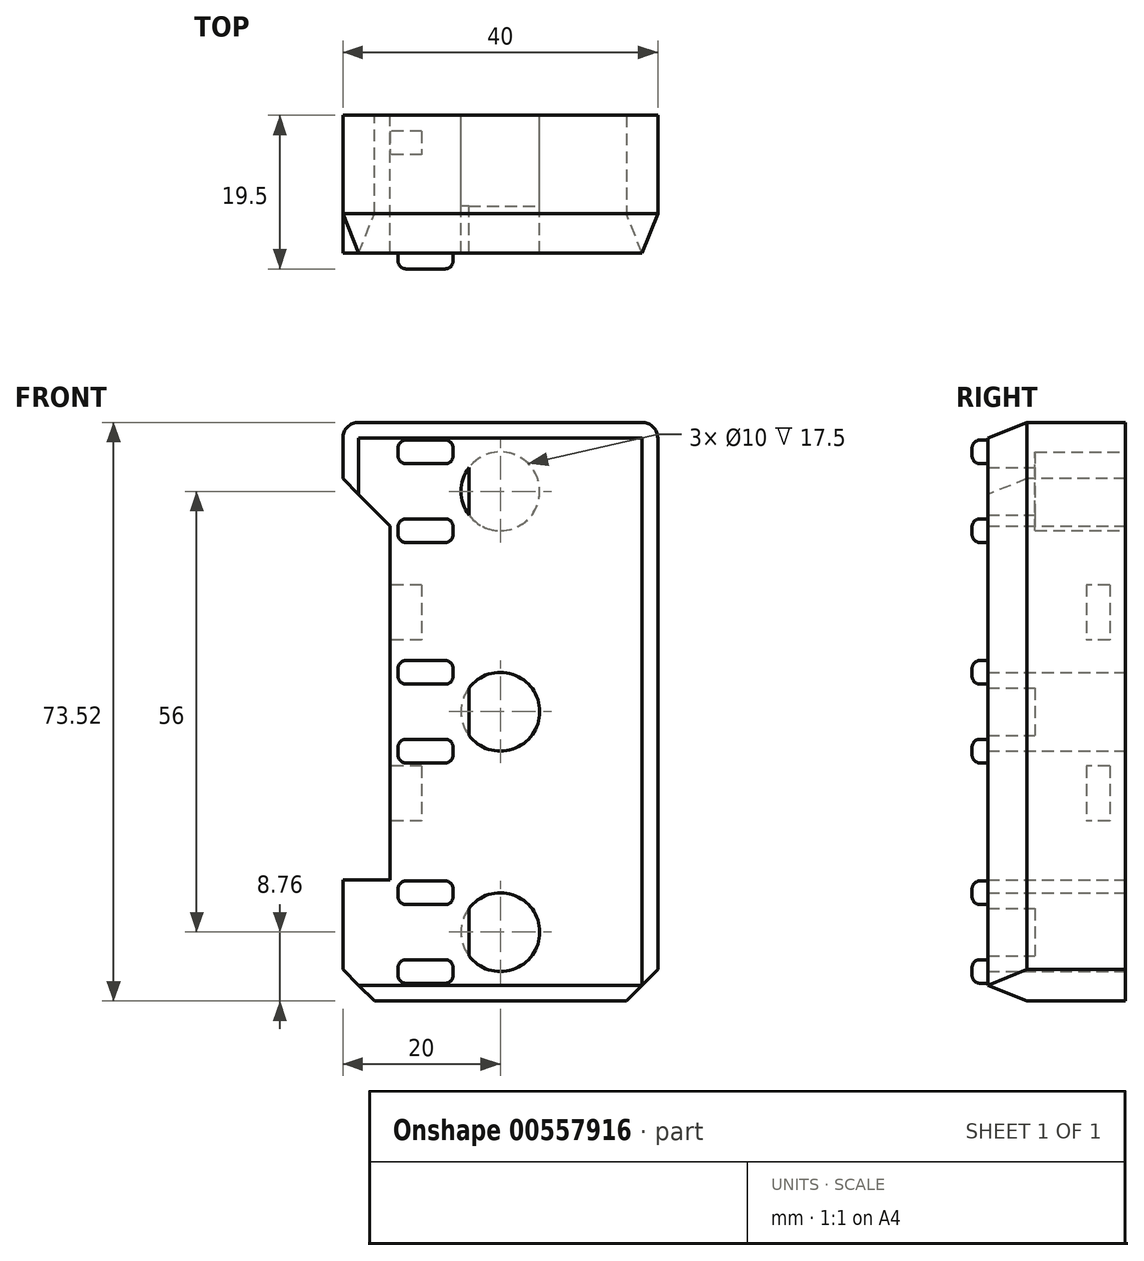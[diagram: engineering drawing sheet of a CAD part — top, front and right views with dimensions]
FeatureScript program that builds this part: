
annotation { "Feature Type Name" : "Feature", "Feature Type Description" : "" }
export const myFeature = defineFeature(function(context is Context, id is Id, definition is map)
    precondition{}
    {
        {
            var Q0;
            Q0=qCreatedBy(makeId("Front.planeOp"),FACE);
            var sketch = newSketch(context, id + "F0", { "sketchPlane" : qUnion([Q0])});
            skLineSegment(sketch, "E0.bottom", {"start": v(-20, 36.76) * mm, "end": v(20, 36.76) * mm});
            skLineSegment(sketch, "E0.top", {"start": v(-20, -36.76) * mm, "end": v(20, -36.76) * mm});
            skLineSegment(sketch, "E0.left", {"start": v(-20, 36.76) * mm, "end": v(-20, -36.76) * mm});
            skLineSegment(sketch, "E0.right", {"start": v(20, 36.76) * mm, "end": v(20, -36.76) * mm});
            skCircle(sketch, "E1", {"center": v(0, 0) * mm, "radius": 5 * mm});
            skCircle(sketch, "E2", {"center": v(0, 28) * mm, "radius": 5 * mm});
            skPoint(sketch, "E2.centerSnap0", {"position": v(0, 36.76) * mm});
            skCircle(sketch, "E3", {"center": v(0, -28) * mm, "radius": 5 * mm});
            skLineSegment(sketch, "E4", {"start": v(-4, 36.76) * mm, "end": v(-4, -36.76) * mm});
            skSolve(sketch);
        }
        {
            var Q0;
            {var subQ4=sQuery(id+"F0.wireOp",EDGE,"E0.left");Q0=makeQuery(id+"F0.imprint","IMPRINT",FACE,{"disambiguationData":[TD([[makeQuery(id+"F0.imprint","IMPRINT",EDGE,{"derivedFrom":subQ4}),1.0]])]});}
            var Q1;
            {var subQ8=sQuery(id+"F0.wireOp",EDGE,"E0.right");Q1=makeQuery(id+"F0.imprint","IMPRINT",FACE,{"disambiguationData":[TD([[makeQuery(id+"F0.imprint","IMPRINT",EDGE,{"derivedFrom":subQ8}),-1.0]])]});}
            var Q2;
            {var subQ0=sQuery(id+"F0.wireOp",EDGE,"E4");var subQ1=sQuery(id+"F0.wireOp",EDGE,"E2");var subQ2=makeQuery(id+"F0.imprint","INTERSECT",VERTEX,{"disambiguationData":[OD(0.0)],"derivedFrom":[subQ1,subQ0]});Q2=makeQuery(id+"F0.imprint","IMPRINT",FACE,{"disambiguationData":[TD([[makeQuery(id+"F0.imprint","IMPRINT",EDGE,{"disambiguationData":[TD([[subQ2,-1.0]])],"derivedFrom":subQ1}),1.0]])]});}
            var Q3;
            {var subQ0=sQuery(id+"F0.wireOp",EDGE,"E4");var subQ1=sQuery(id+"F0.wireOp",EDGE,"E1");var subQ2=makeQuery(id+"F0.imprint","INTERSECT",VERTEX,{"disambiguationData":[OD(0.0)],"derivedFrom":[subQ1,subQ0]});Q3=makeQuery(id+"F0.imprint","IMPRINT",FACE,{"disambiguationData":[TD([[makeQuery(id+"F0.imprint","IMPRINT",EDGE,{"disambiguationData":[TD([[subQ2,-1.0]])],"derivedFrom":subQ1}),1.0]])]});}
            var Q4;
            {var subQ0=sQuery(id+"F0.wireOp",EDGE,"E4");var subQ1=sQuery(id+"F0.wireOp",EDGE,"E3");var subQ2=makeQuery(id+"F0.imprint","INTERSECT",VERTEX,{"disambiguationData":[OD(0.0)],"derivedFrom":[subQ1,subQ0]});Q4=makeQuery(id+"F0.imprint","IMPRINT",FACE,{"disambiguationData":[TD([[makeQuery(id+"F0.imprint","IMPRINT",EDGE,{"disambiguationData":[TD([[subQ2,-1.0]])],"derivedFrom":subQ1}),1.0]])]});}
            extrude(context, id + "F1", {"entities" : qUnion([Q0, Q1, Q2, Q3, Q4]), "depth" : 6 * mm, "offsetDistance" : 25 * mm});
        }
        {
            var Q0;
            {var subQ8=sQuery(id+"F0.wireOp",EDGE,"E0.right");Q0=makeQuery(id+"F0.imprint","IMPRINT",FACE,{"disambiguationData":[TD([[makeQuery(id+"F0.imprint","IMPRINT",EDGE,{"derivedFrom":subQ8}),-1.0]])]});}
            var Q1;
            {var subQ4=sQuery(id+"F0.wireOp",EDGE,"E0.left");Q1=makeQuery(id+"F0.imprint","IMPRINT",FACE,{"disambiguationData":[TD([[makeQuery(id+"F0.imprint","IMPRINT",EDGE,{"derivedFrom":subQ4}),1.0]])]});}
            extrude(context, id + "F2", {"entities" : qUnion([Q0, Q1]), "operationType" : NewBodyOperationType.ADD, "oppositeDirection" : true, "depth" : 11.5 * mm, "offsetDistance" : 25 * mm});
        }
        {
            var Q0;
            {var subQ0=sQuery(id+"F0.wireOp",EDGE,"E0.right");var subQ1=sQuery(id+"F0.wireOp",EDGE,"E0.top");Q0=makeQuery(id+"F2.boolean.opBoolean","MERGE",EDGE,{"derivedFrom":[makeQuery(id+"F1.opExtrude","SWEPT_EDGE",EDGE,{"disambiguationData":[OSD([subQ1,subQ0])]}),makeQuery(id+"F2.opExtrude","SWEPT_EDGE",EDGE,{"disambiguationData":[OSD([subQ1,subQ0])]})]});}
            var Q1;
            {var subQ0=sQuery(id+"F0.wireOp",EDGE,"E0.left");var subQ1=sQuery(id+"F0.wireOp",EDGE,"E0.top");Q1=makeQuery(id+"F2.boolean.opBoolean","MERGE",EDGE,{"derivedFrom":[makeQuery(id+"F1.opExtrude","SWEPT_EDGE",EDGE,{"disambiguationData":[OSD([subQ1,subQ0])]}),makeQuery(id+"F2.opExtrude","SWEPT_EDGE",EDGE,{"disambiguationData":[OSD([subQ1,subQ0])]})]});}
            chamfer(context, id + "F3", {"entities" : qUnion([Q0, Q1]), "width" : 4 * mm, "tangentPropagation" : true});
        }
        {
            var Q0;
            Q0=qCreatedBy(makeId("Front.planeOp"),FACE);
            var sketch = newSketch(context, id + "F4", { "sketchPlane" : qUnion([Q0])});
            skLineSegment(sketch, "E5.bottom", {"start": v(-20, 23.61) * mm, "end": v(-14, 23.61) * mm});
            skLineSegment(sketch, "E5.top", {"start": v(-20, -21.39) * mm, "end": v(-14, -21.39) * mm});
            skLineSegment(sketch, "E5.left", {"start": v(-20, 23.61) * mm, "end": v(-20, -21.39) * mm});
            skLineSegment(sketch, "E5.right", {"start": v(-14, 23.61) * mm, "end": v(-14, -21.39) * mm});
            skSolve(sketch);
        }
        {
            var Q0;
            Q0 = qSketchRegion(id + "F4", true);
            extrude(context, id + "F5", {"entities" : qUnion([Q0]), "operationType" : NewBodyOperationType.REMOVE, "endBound" : BoundingType.SYMMETRIC, "depth" : 50 * mm, "offsetDistance" : 25 * mm});
        }
        {
            var Q0;
            Q0=makeQuery(id+"F5.boolean.opBoolean","COPY",EDGE,{"derivedFrom":makeQuery(id+"F5.opExtrude","SWEPT_EDGE",EDGE,{"disambiguationData":[OSD([sQuery(id+"F4.wireOp",EDGE,"E5.bottom"),sQuery(id+"F4.wireOp",EDGE,"E5.left")])]})});
            var Q1;
            Q1=makeQuery(id+"F5.boolean.opBoolean","COPY",EDGE,{"derivedFrom":makeQuery(id+"F5.opExtrude","SWEPT_EDGE",EDGE,{"disambiguationData":[OSD([sQuery(id+"F4.wireOp",EDGE,"E5.top"),sQuery(id+"F4.wireOp",EDGE,"E5.left")])]})});
            chamfer(context, id + "F6", {"entities" : qUnion([Q0, Q1]), "width" : 6 * mm, "tangentPropagation" : true});
        }
        {
            var Q0;
            Q0=qCreatedBy(makeId("Right.planeOp"),FACE);
            var sketch = newSketch(context, id + "F7", { "sketchPlane" : qUnion([Q0])});
            skLineSegment(sketch, "E6.bottom", {"start": v(-6, 34.5) * mm, "end": v(-8, 34.5) * mm});
            skLineSegment(sketch, "E6.top", {"start": v(-6, 31.5) * mm, "end": v(-8, 31.5) * mm});
            skLineSegment(sketch, "E6.left", {"start": v(-6, 34.5) * mm, "end": v(-6, 31.5) * mm});
            skLineSegment(sketch, "E6.right", {"start": v(-8, 34.5) * mm, "end": v(-8, 31.5) * mm});
            skLineSegment(sketch, "E7.bottom", {"start": v(-6, 24.5) * mm, "end": v(-8, 24.5) * mm});
            skLineSegment(sketch, "E7.top", {"start": v(-6, 21.5) * mm, "end": v(-8, 21.5) * mm});
            skLineSegment(sketch, "E7.left", {"start": v(-6, 24.5) * mm, "end": v(-6, 21.5) * mm});
            skLineSegment(sketch, "E7.right", {"start": v(-8, 24.5) * mm, "end": v(-8, 21.5) * mm});
            skLineSegment(sketch, "E8.bottom", {"start": v(-6, 6.5) * mm, "end": v(-8, 6.5) * mm});
            skLineSegment(sketch, "E8.top", {"start": v(-6, 3.5) * mm, "end": v(-8, 3.5) * mm});
            skLineSegment(sketch, "E8.left", {"start": v(-6, 6.5) * mm, "end": v(-6, 3.5) * mm});
            skLineSegment(sketch, "E8.right", {"start": v(-8, 6.5) * mm, "end": v(-8, 3.5) * mm});
            skLineSegment(sketch, "E9.bottom", {"start": v(-6, -3.5) * mm, "end": v(-8, -3.5) * mm});
            skLineSegment(sketch, "E9.top", {"start": v(-6, -6.5) * mm, "end": v(-8, -6.5) * mm});
            skLineSegment(sketch, "E9.left", {"start": v(-6, -3.5) * mm, "end": v(-6, -6.5) * mm});
            skLineSegment(sketch, "E9.right", {"start": v(-8, -3.5) * mm, "end": v(-8, -6.5) * mm});
            skLineSegment(sketch, "E10.bottom", {"start": v(-6, -21.5) * mm, "end": v(-8, -21.5) * mm});
            skLineSegment(sketch, "E10.top", {"start": v(-6, -24.5) * mm, "end": v(-8, -24.5) * mm});
            skLineSegment(sketch, "E10.left", {"start": v(-6, -21.5) * mm, "end": v(-6, -24.5) * mm});
            skLineSegment(sketch, "E10.right", {"start": v(-8, -21.5) * mm, "end": v(-8, -24.5) * mm});
            skLineSegment(sketch, "E11.bottom", {"start": v(-6, -31.5) * mm, "end": v(-8, -31.5) * mm});
            skLineSegment(sketch, "E11.top", {"start": v(-6, -34.5) * mm, "end": v(-8, -34.5) * mm});
            skLineSegment(sketch, "E11.left", {"start": v(-6, -31.5) * mm, "end": v(-6, -34.5) * mm});
            skLineSegment(sketch, "E11.right", {"start": v(-8, -31.5) * mm, "end": v(-8, -34.5) * mm});
            skSolve(sketch);
        }
        {
            var Q0;
            Q0 = qSketchRegion(id + "F7", true);
            extrude(context, id + "F8", {"entities" : qUnion([Q0]), "operationType" : NewBodyOperationType.ADD, "oppositeDirection" : true, "depth" : 13 * mm, "offsetDistance" : 25 * mm, "hasSecondDirection" : true, "secondDirectionOppositeDirection" : true, "secondDirectionDepth" : 6 * mm});
        }
        {
            var Q0;
            Q0=makeQuery(id+"F8.opExtrude","CAP_EDGE",EDGE,{"disambiguationData":[OSD([sQuery(id+"F7.wireOp",EDGE,"E11.top")])],"isStart":false});
            fillet(context, id + "F9", {"entities" : qUnion([Q0]), "radius" : 1 * mm, "tangentPropagation" : true, "allowEdgeOverflow" : false});
        }
        {
            var Q0;
            Q0=makeQuery(id+"F8.opExtrude","CAP_EDGE",EDGE,{"disambiguationData":[OSD([sQuery(id+"F7.wireOp",EDGE,"E11.top")])],"isStart":true});
            var Q1;
            Q1=makeQuery(id+"F8.opExtrude","CAP_EDGE",EDGE,{"disambiguationData":[OSD([sQuery(id+"F7.wireOp",EDGE,"E11.bottom")])],"isStart":false});
            var Q2;
            Q2=makeQuery(id+"F8.opExtrude","CAP_EDGE",EDGE,{"disambiguationData":[OSD([sQuery(id+"F7.wireOp",EDGE,"E11.bottom")])],"isStart":true});
            var Q3;
            Q3=makeQuery(id+"F8.opExtrude","SWEPT_EDGE",EDGE,{"disambiguationData":[OSD([sQuery(id+"F7.wireOp",EDGE,"E11.bottom"),sQuery(id+"F7.wireOp",EDGE,"E11.right")])]});
            var Q4;
            Q4=makeQuery(id+"F8.opExtrude","SWEPT_EDGE",EDGE,{"disambiguationData":[OSD([sQuery(id+"F7.wireOp",EDGE,"E11.top"),sQuery(id+"F7.wireOp",EDGE,"E11.right")])]});
            var Q5;
            Q5=makeQuery(id+"F8.opExtrude","CAP_EDGE",EDGE,{"disambiguationData":[OSD([sQuery(id+"F7.wireOp",EDGE,"E11.right")])],"isStart":true});
            var Q6;
            Q6=makeQuery(id+"F8.opExtrude","CAP_EDGE",EDGE,{"disambiguationData":[OSD([sQuery(id+"F7.wireOp",EDGE,"E10.top")])],"isStart":true});
            var Q7;
            Q7=makeQuery(id+"F8.opExtrude","CAP_EDGE",EDGE,{"disambiguationData":[OSD([sQuery(id+"F7.wireOp",EDGE,"E10.top")])],"isStart":false});
            var Q8;
            Q8=makeQuery(id+"F8.opExtrude","CAP_EDGE",EDGE,{"disambiguationData":[OSD([sQuery(id+"F7.wireOp",EDGE,"E10.bottom")])],"isStart":false});
            var Q9;
            Q9=makeQuery(id+"F8.opExtrude","CAP_EDGE",EDGE,{"disambiguationData":[OSD([sQuery(id+"F7.wireOp",EDGE,"E10.bottom")])],"isStart":true});
            var Q10;
            Q10=makeQuery(id+"F8.opExtrude","SWEPT_EDGE",EDGE,{"disambiguationData":[OSD([sQuery(id+"F7.wireOp",EDGE,"E10.bottom"),sQuery(id+"F7.wireOp",EDGE,"E10.right")])]});
            var Q11;
            Q11=makeQuery(id+"F8.opExtrude","SWEPT_EDGE",EDGE,{"disambiguationData":[OSD([sQuery(id+"F7.wireOp",EDGE,"E10.top"),sQuery(id+"F7.wireOp",EDGE,"E10.right")])]});
            var Q12;
            Q12=makeQuery(id+"F8.opExtrude","CAP_EDGE",EDGE,{"disambiguationData":[OSD([sQuery(id+"F7.wireOp",EDGE,"E10.right")])],"isStart":true});
            var Q13;
            Q13=makeQuery(id+"F8.opExtrude","CAP_EDGE",EDGE,{"disambiguationData":[OSD([sQuery(id+"F7.wireOp",EDGE,"E10.right")])],"isStart":false});
            var Q14;
            Q14=makeQuery(id+"F8.opExtrude","CAP_EDGE",EDGE,{"disambiguationData":[OSD([sQuery(id+"F7.wireOp",EDGE,"E9.top")])],"isStart":true});
            var Q15;
            Q15=makeQuery(id+"F8.opExtrude","CAP_EDGE",EDGE,{"disambiguationData":[OSD([sQuery(id+"F7.wireOp",EDGE,"E9.top")])],"isStart":false});
            var Q16;
            Q16=makeQuery(id+"F8.opExtrude","CAP_EDGE",EDGE,{"disambiguationData":[OSD([sQuery(id+"F7.wireOp",EDGE,"E9.bottom")])],"isStart":false});
            var Q17;
            Q17=makeQuery(id+"F8.opExtrude","CAP_EDGE",EDGE,{"disambiguationData":[OSD([sQuery(id+"F7.wireOp",EDGE,"E9.bottom")])],"isStart":true});
            var Q18;
            Q18=makeQuery(id+"F8.opExtrude","SWEPT_EDGE",EDGE,{"disambiguationData":[OSD([sQuery(id+"F7.wireOp",EDGE,"E9.top"),sQuery(id+"F7.wireOp",EDGE,"E9.right")])]});
            var Q19;
            Q19=makeQuery(id+"F8.opExtrude","SWEPT_EDGE",EDGE,{"disambiguationData":[OSD([sQuery(id+"F7.wireOp",EDGE,"E9.bottom"),sQuery(id+"F7.wireOp",EDGE,"E9.right")])]});
            var Q20;
            Q20=makeQuery(id+"F8.opExtrude","CAP_EDGE",EDGE,{"disambiguationData":[OSD([sQuery(id+"F7.wireOp",EDGE,"E9.right")])],"isStart":true});
            var Q21;
            Q21=makeQuery(id+"F8.opExtrude","CAP_EDGE",EDGE,{"disambiguationData":[OSD([sQuery(id+"F7.wireOp",EDGE,"E9.right")])],"isStart":false});
            var Q22;
            Q22=makeQuery(id+"F8.opExtrude","CAP_EDGE",EDGE,{"disambiguationData":[OSD([sQuery(id+"F7.wireOp",EDGE,"E8.top")])],"isStart":false});
            var Q23;
            Q23=makeQuery(id+"F8.opExtrude","CAP_EDGE",EDGE,{"disambiguationData":[OSD([sQuery(id+"F7.wireOp",EDGE,"E8.top")])],"isStart":true});
            var Q24;
            Q24=makeQuery(id+"F8.opExtrude","CAP_EDGE",EDGE,{"disambiguationData":[OSD([sQuery(id+"F7.wireOp",EDGE,"E8.bottom")])],"isStart":true});
            var Q25;
            Q25=makeQuery(id+"F8.opExtrude","CAP_EDGE",EDGE,{"disambiguationData":[OSD([sQuery(id+"F7.wireOp",EDGE,"E8.bottom")])],"isStart":false});
            var Q26;
            Q26=makeQuery(id+"F8.opExtrude","SWEPT_EDGE",EDGE,{"disambiguationData":[OSD([sQuery(id+"F7.wireOp",EDGE,"E8.bottom"),sQuery(id+"F7.wireOp",EDGE,"E8.right")])]});
            var Q27;
            Q27=makeQuery(id+"F8.opExtrude","SWEPT_EDGE",EDGE,{"disambiguationData":[OSD([sQuery(id+"F7.wireOp",EDGE,"E8.top"),sQuery(id+"F7.wireOp",EDGE,"E8.right")])]});
            var Q28;
            Q28=makeQuery(id+"F8.opExtrude","CAP_EDGE",EDGE,{"disambiguationData":[OSD([sQuery(id+"F7.wireOp",EDGE,"E8.right")])],"isStart":false});
            var Q29;
            Q29=makeQuery(id+"F8.opExtrude","CAP_EDGE",EDGE,{"disambiguationData":[OSD([sQuery(id+"F7.wireOp",EDGE,"E8.right")])],"isStart":true});
            var Q30;
            Q30=makeQuery(id+"F8.opExtrude","CAP_EDGE",EDGE,{"disambiguationData":[OSD([sQuery(id+"F7.wireOp",EDGE,"E7.top")])],"isStart":false});
            var Q31;
            Q31=makeQuery(id+"F8.opExtrude","CAP_EDGE",EDGE,{"disambiguationData":[OSD([sQuery(id+"F7.wireOp",EDGE,"E7.top")])],"isStart":true});
            var Q32;
            Q32=makeQuery(id+"F8.opExtrude","CAP_EDGE",EDGE,{"disambiguationData":[OSD([sQuery(id+"F7.wireOp",EDGE,"E7.bottom")])],"isStart":true});
            var Q33;
            Q33=makeQuery(id+"F8.opExtrude","CAP_EDGE",EDGE,{"disambiguationData":[OSD([sQuery(id+"F7.wireOp",EDGE,"E7.bottom")])],"isStart":false});
            var Q34;
            Q34=makeQuery(id+"F8.opExtrude","SWEPT_EDGE",EDGE,{"disambiguationData":[OSD([sQuery(id+"F7.wireOp",EDGE,"E7.bottom"),sQuery(id+"F7.wireOp",EDGE,"E7.right")])]});
            var Q35;
            Q35=makeQuery(id+"F8.opExtrude","SWEPT_EDGE",EDGE,{"disambiguationData":[OSD([sQuery(id+"F7.wireOp",EDGE,"E7.top"),sQuery(id+"F7.wireOp",EDGE,"E7.right")])]});
            var Q36;
            Q36=makeQuery(id+"F8.opExtrude","CAP_EDGE",EDGE,{"disambiguationData":[OSD([sQuery(id+"F7.wireOp",EDGE,"E7.right")])],"isStart":true});
            var Q37;
            Q37=makeQuery(id+"F8.opExtrude","CAP_EDGE",EDGE,{"disambiguationData":[OSD([sQuery(id+"F7.wireOp",EDGE,"E7.right")])],"isStart":false});
            var Q38;
            Q38=makeQuery(id+"F8.opExtrude","SWEPT_EDGE",EDGE,{"disambiguationData":[OSD([sQuery(id+"F7.wireOp",EDGE,"E6.top"),sQuery(id+"F7.wireOp",EDGE,"E6.right")])]});
            var Q39;
            Q39=makeQuery(id+"F8.opExtrude","CAP_EDGE",EDGE,{"disambiguationData":[OSD([sQuery(id+"F7.wireOp",EDGE,"E6.top")])],"isStart":false});
            var Q40;
            Q40=makeQuery(id+"F8.opExtrude","CAP_EDGE",EDGE,{"disambiguationData":[OSD([sQuery(id+"F7.wireOp",EDGE,"E6.top")])],"isStart":true});
            var Q41;
            Q41=makeQuery(id+"F8.opExtrude","CAP_EDGE",EDGE,{"disambiguationData":[OSD([sQuery(id+"F7.wireOp",EDGE,"E6.right")])],"isStart":true});
            var Q42;
            Q42=makeQuery(id+"F8.opExtrude","CAP_EDGE",EDGE,{"disambiguationData":[OSD([sQuery(id+"F7.wireOp",EDGE,"E6.right")])],"isStart":false});
            var Q43;
            Q43=makeQuery(id+"F8.opExtrude","SWEPT_EDGE",EDGE,{"disambiguationData":[OSD([sQuery(id+"F7.wireOp",EDGE,"E6.bottom"),sQuery(id+"F7.wireOp",EDGE,"E6.right")])]});
            var Q44;
            Q44=makeQuery(id+"F8.opExtrude","CAP_EDGE",EDGE,{"disambiguationData":[OSD([sQuery(id+"F7.wireOp",EDGE,"E6.bottom")])],"isStart":false});
            var Q45;
            Q45=makeQuery(id+"F8.opExtrude","CAP_EDGE",EDGE,{"disambiguationData":[OSD([sQuery(id+"F7.wireOp",EDGE,"E6.bottom")])],"isStart":true});
            fillet(context, id + "F10", {"entities" : qUnion([Q0, Q1, Q2, Q3, Q4, Q5, Q6, Q7, Q8, Q9, Q10, Q11, Q12, Q13, Q14, Q15, Q16, Q17, Q18, Q19, Q20, Q21, Q22, Q23, Q24, Q25, Q26, Q27, Q28, Q29, Q30, Q31, Q32, Q33, Q34, Q35, Q36, Q37, Q38, Q39, Q40, Q41, Q42, Q43, Q44, Q45]), "radius" : 1 * mm, "tangentPropagation" : true, "allowEdgeOverflow" : false});
        }
        {
            var Q0;
            {var subQ0=sQuery(id+"F0.wireOp",EDGE,"E0.left");var subQ1=sQuery(id+"F0.wireOp",EDGE,"E0.bottom");Q0=makeQuery(id+"F2.boolean.opBoolean","MERGE",EDGE,{"derivedFrom":[makeQuery(id+"F1.opExtrude","SWEPT_EDGE",EDGE,{"disambiguationData":[OSD([subQ1,subQ0])]}),makeQuery(id+"F2.opExtrude","SWEPT_EDGE",EDGE,{"disambiguationData":[OSD([subQ1,subQ0])]})]});}
            var Q1;
            {var subQ0=sQuery(id+"F0.wireOp",EDGE,"E0.right");var subQ1=sQuery(id+"F0.wireOp",EDGE,"E0.bottom");Q1=makeQuery(id+"F2.boolean.opBoolean","MERGE",EDGE,{"derivedFrom":[makeQuery(id+"F1.opExtrude","SWEPT_EDGE",EDGE,{"disambiguationData":[OSD([subQ1,subQ0])]}),makeQuery(id+"F2.opExtrude","SWEPT_EDGE",EDGE,{"disambiguationData":[OSD([subQ1,subQ0])]})]});}
            fillet(context, id + "F11", {"entities" : qUnion([Q0, Q1]), "radius" : 2 * mm, "tangentPropagation" : true, "allowEdgeOverflow" : false});
        }
        {
            var Q0;
            Q0=makeQuery(id+"F1.opExtrude","CAP_EDGE",EDGE,{"disambiguationData":[OSD([sQuery(id+"F0.wireOp",EDGE,"E0.right")])],"isStart":false});
            var Q1;
            Q1=makeQuery(id+"F1.opExtrude","CAP_EDGE",EDGE,{"disambiguationData":[OSD([sQuery(id+"F0.wireOp",EDGE,"E0.top")])],"isStart":false});
            chamfer(context, id + "F12", {"entities" : qUnion([Q0, Q1]), "chamferType" : ChamferType.TWO_OFFSETS, "width1" : 5 * mm, "oppositeDirection" : false, "width2" : 2 * mm, "tangentPropagation" : true});
        }
        {
            var Q0;
            Q0=makeQuery(id+"F5.boolean.opBoolean","COPY",FACE,{"derivedFrom":makeQuery(id+"F5.opExtrude","SWEPT_FACE",FACE,{"disambiguationData":[OSD([sQuery(id+"F4.wireOp",EDGE,"E5.right")])]})});
            var sketch = newSketch(context, id + "F13", { "sketchPlane" : qUnion([Q0])});
            skLineSegment(sketch, "E12.bottom", {"start": v(-9.5, 16.11) * mm, "end": v(-6.5, 16.11) * mm});
            skLineSegment(sketch, "E12.top", {"start": v(-9.5, 9.11) * mm, "end": v(-6.5, 9.11) * mm});
            skLineSegment(sketch, "E12.left", {"start": v(-9.5, 16.11) * mm, "end": v(-9.5, 9.11) * mm});
            skLineSegment(sketch, "E12.right", {"start": v(-6.5, 16.11) * mm, "end": v(-6.5, 9.11) * mm});
            skLineSegment(sketch, "E13.bottom", {"start": v(-9.5, -6.89) * mm, "end": v(-6.5, -6.89) * mm});
            skLineSegment(sketch, "E13.top", {"start": v(-9.5, -13.89) * mm, "end": v(-6.5, -13.89) * mm});
            skLineSegment(sketch, "E13.left", {"start": v(-9.5, -6.89) * mm, "end": v(-9.5, -13.89) * mm});
            skLineSegment(sketch, "E13.right", {"start": v(-6.5, -6.89) * mm, "end": v(-6.5, -13.89) * mm});
            skLineSegment(sketch, "E14", {"start": v(6, 23.61) * mm, "end": v(6, -21.39) * mm});
            skLineSegment(sketch, "E15", {"start": v(6, -21.39) * mm, "end": v(-11.5, -21.39) * mm});
            skSolve(sketch);
        }
        {
            var Q0;
            Q0 = qSketchRegion(id + "F13", true);
            extrude(context, id + "F14", {"entities" : qUnion([Q0]), "operationType" : NewBodyOperationType.REMOVE, "oppositeDirection" : true, "depth" : 4 * mm, "offsetDistance" : 25 * mm});
        }
    });
